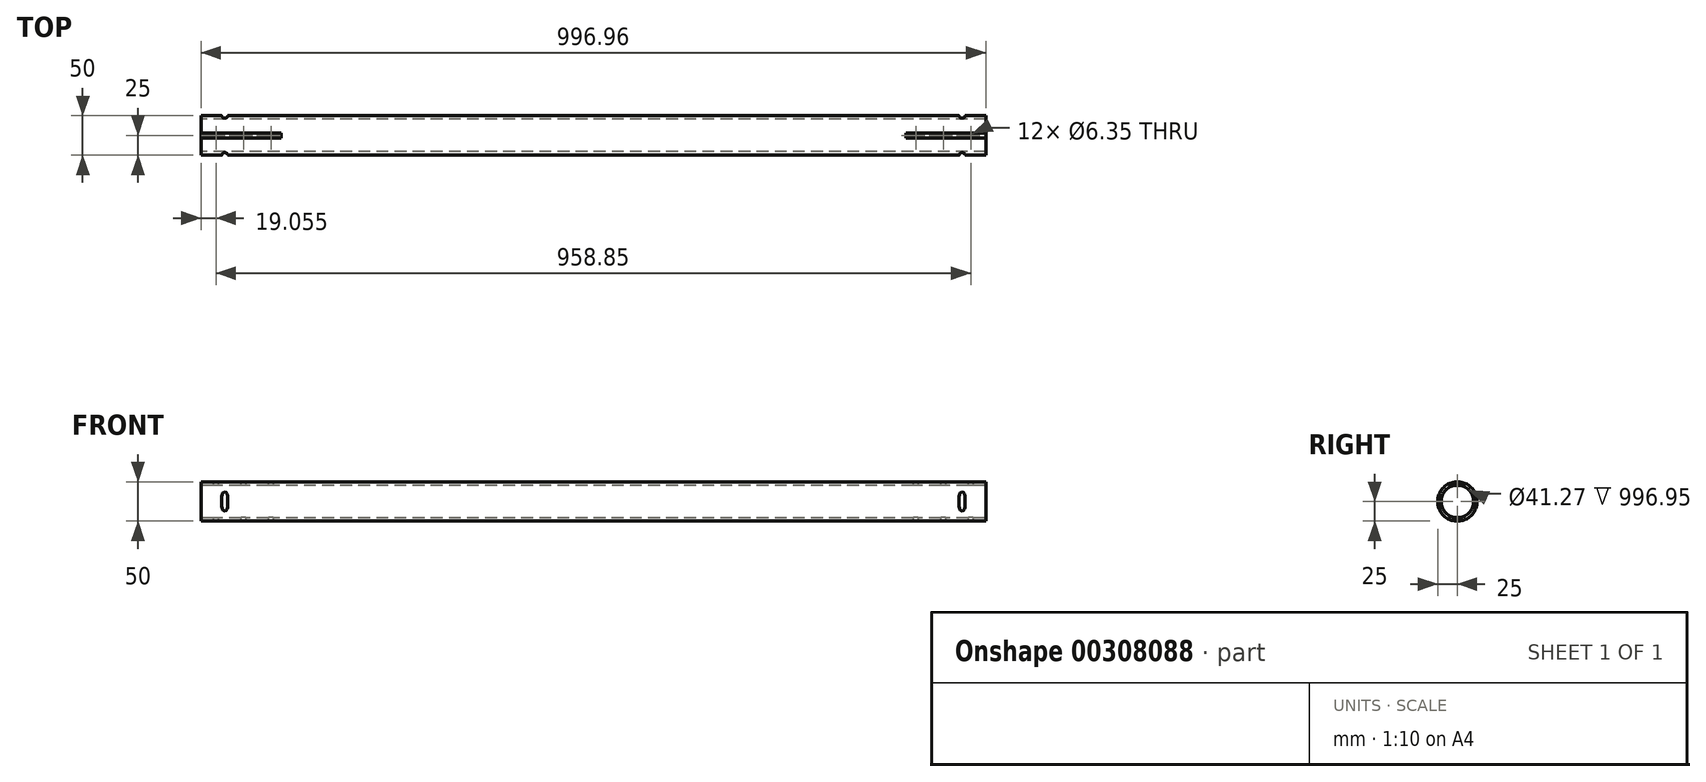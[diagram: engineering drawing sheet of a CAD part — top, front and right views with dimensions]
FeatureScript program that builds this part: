
annotation { "Feature Type Name" : "Feature", "Feature Type Description" : "" }
export const myFeature = defineFeature(function(context is Context, id is Id, definition is map)
    precondition{}
    {
        {
            var Q0;
            Q0=qCreatedBy(makeId("Right.planeOp"),FACE);
            var sketch = newSketch(context, id + "F0", { "sketchPlane" : qUnion([Q0])});
            skCircle(sketch, "E0", {"center": v(0, 0) * mm, "radius": 20.64 * mm});
            skCircle(sketch, "E1", {"center": v(0, 0) * mm, "radius": 25 * mm});
            skSolve(sketch);
        }
        {
            var Q0;
            Q0=qSketchRegion(id+"F0",true);
            extrude(context, id + "F1", {"entities" : qUnion([Q0]), "endBound" : BoundingType.SYMMETRIC, "depth" : 996.95 * mm, "offsetDistance" : 25.4 * mm});
        }
        {
            var Q0;
            Q0=makeQuery(id+"F1.opExtrude","CAP_FACE",FACE,{"disambiguationData":[OSD([sQuery(id+"F0.wireOp",EDGE,"E0"),sQuery(id+"F0.wireOp",EDGE,"E1")])],"isStart":false});
            var sketch = newSketch(context, id + "F2", { "sketchPlane" : qUnion([Q0])});
            skLineSegment(sketch, "E2", {"start": v(-25, 0) * mm, "end": v(25, 0) * mm, "construction": true});
            skLineSegment(sketch, "E3.bottom", {"start": v(-3.17, 26.39) * mm, "end": v(3.18, 26.39) * mm});
            skLineSegment(sketch, "E3.top", {"start": v(-3.17, 24.8) * mm, "end": v(3.18, 24.8) * mm});
            skLineSegment(sketch, "E3.left", {"start": v(-3.17, 26.39) * mm, "end": v(-3.17, 24.8) * mm});
            skLineSegment(sketch, "E3.right", {"start": v(3.18, 26.39) * mm, "end": v(3.18, 24.8) * mm});
            skLineSegment(sketch, "E4.MirrorCS", {"start": v(3.18, -26.39) * mm, "end": v(3.18, -24.8) * mm});
            skLineSegment(sketch, "E5.MirrorCS", {"start": v(-3.17, -26.39) * mm, "end": v(-3.17, -24.8) * mm});
            skLineSegment(sketch, "E6.MirrorCS", {"start": v(-3.17, -24.8) * mm, "end": v(3.18, -24.8) * mm});
            skLineSegment(sketch, "E7.MirrorCS", {"start": v(-3.17, -26.39) * mm, "end": v(3.18, -26.39) * mm});
            skSolve(sketch);
        }
        {
            var Q0;
            Q0=qSketchRegion(id+"F2",true);
            extrude(context, id + "F3", {"entities" : qUnion([Q0]), "operationType" : NewBodyOperationType.REMOVE, "oppositeDirection" : true, "depth" : 101.6 * mm, "offsetDistance" : 25.4 * mm});
        }
        {
            var Q0;
            Q0=makeQuery(id+"F1.opExtrude","CAP_FACE",FACE,{"disambiguationData":[OSD([sQuery(id+"F0.wireOp",EDGE,"E0"),sQuery(id+"F0.wireOp",EDGE,"E1")])],"isStart":true});
            var sketch = newSketch(context, id + "F4", { "sketchPlane" : qUnion([Q0])});
            skLineSegment(sketch, "E8.bottom", {"start": v(-3.17, 26.39) * mm, "end": v(3.18, 26.39) * mm});
            skLineSegment(sketch, "E8.top", {"start": v(-3.17, 24.8) * mm, "end": v(3.18, 24.8) * mm});
            skLineSegment(sketch, "E8.left", {"start": v(-3.17, 26.39) * mm, "end": v(-3.17, 24.8) * mm});
            skLineSegment(sketch, "E8.right", {"start": v(3.18, 26.39) * mm, "end": v(3.18, 24.8) * mm});
            skLineSegment(sketch, "E9", {"start": v(-25, 0) * mm, "end": v(25, 0) * mm, "construction": true});
            skLineSegment(sketch, "E10.MirrorCS", {"start": v(-3.17, -26.39) * mm, "end": v(-3.17, -24.8) * mm});
            skLineSegment(sketch, "E11.MirrorCS", {"start": v(3.18, -26.39) * mm, "end": v(3.18, -24.8) * mm});
            skLineSegment(sketch, "E12.MirrorCS", {"start": v(-3.17, -26.39) * mm, "end": v(3.18, -26.39) * mm});
            skLineSegment(sketch, "E13.MirrorCS", {"start": v(-3.17, -24.8) * mm, "end": v(3.18, -24.8) * mm});
            skSolve(sketch);
        }
        {
            var Q0;
            Q0=qSketchRegion(id+"F4",true);
            extrude(context, id + "F5", {"entities" : qUnion([Q0]), "operationType" : NewBodyOperationType.REMOVE, "oppositeDirection" : true, "depth" : 101.6 * mm, "offsetDistance" : 25.4 * mm});
        }
        {
            var Q0;
            Q0=makeQuery(id+"F5.boolean.opBoolean","COPY",FACE,{"derivedFrom":makeQuery(id+"F5.opExtrude","SWEPT_FACE",FACE,{"disambiguationData":[OSD([sQuery(id+"F4.wireOp",EDGE,"E8.top")])]})});
            var sketch = newSketch(context, id + "F6", { "sketchPlane" : qUnion([Q0])});
            skLineSegment(sketch, "E14", {"start": v(-498.48, 0) * mm, "end": v(-409.58, 0) * mm, "construction": true});
            skPoint(sketch, "E15", {"position": v(-479.43, 0) * mm});
            skPoint(sketch, "E16", {"position": v(-444.5, 0) * mm});
            skPoint(sketch, "E17", {"position": v(-409.58, 0) * mm});
            skLineSegment(sketch, "E18.MirrorCS", {"start": v(498.48, 0) * mm, "end": v(409.58, 0) * mm, "construction": true});
            skPoint(sketch, "E19.MirrorP", {"position": v(444.5, 0) * mm});
            skPoint(sketch, "E20.MirrorP", {"position": v(479.43, 0) * mm});
            skPoint(sketch, "E21.MirrorP", {"position": v(409.58, 0) * mm});
            skSolve(sketch);
        }
        {
            var Q0;
            Q0=sQuery(id+"F6.wireOp",VERTEX,"E15");
            var Q1;
            Q1=sQuery(id+"F6.wireOp",VERTEX,"E16");
            var Q2;
            Q2=sQuery(id+"F6.wireOp",VERTEX,"E17");
            var Q3;
            Q3=sQuery(id+"F6.wireOp",VERTEX,"E21.MirrorP");
            var Q4;
            Q4=sQuery(id+"F6.wireOp",VERTEX,"E19.MirrorP");
            var Q5;
            Q5=sQuery(id+"F6.wireOp",VERTEX,"E20.MirrorP");
            var Q6;
            Q6=makeQuery(id+"F1.opExtrude","SWEPT_BODY",BODY,{"disambiguationData":[OSD([sQuery(id+"F0.wireOp",EDGE,"E0"),sQuery(id+"F0.wireOp",EDGE,"E1")])]});
            hole(context, id + "F7", {"style" : HoleStyle.SIMPLE, "endStyle" : HoleEndStyle.THROUGH, "holeDiameter" : 6.35 * mm, "majorDiameter" : 6.35 * mm, "isTappedThrough" : true, "tappedDepth" : 12.7 * mm, "tapClearance" : 3, "locations" : qUnion([Q0, Q1, Q2, Q3, Q4, Q5]), "scope" : qUnion([Q6])});
        }
        {
            var Q0;
            {var subQ0=sQuery(id+"F0.wireOp",EDGE,"E1");var subQ1=makeQuery(id+"F5.boolean.opBoolean","COPY",FACE,{"derivedFrom":makeQuery(id+"F5.opExtrude","SWEPT_FACE",FACE,{"disambiguationData":[OSD([sQuery(id+"F4.wireOp",EDGE,"E8.top")])]})});Q0=makeQuery(id+"F7.hole-0.boolean.opBoolean","SPLIT",FACE,{"disambiguationData":[TD([makeQuery(id+"F1.opExtrude","CAP_FACE",FACE,{"disambiguationData":[OSD([sQuery(id+"F0.wireOp",EDGE,"E0"),subQ0])],"isStart":true})])],"derivedFrom":subQ1});}
            var sketch = newSketch(context, id + "F8", { "sketchPlane" : qUnion([Q0])});
            skCircle(sketch, "E22", {"center": v(-468.31, 25.8) * mm, "radius": 3.97 * mm});
            skCircle(sketch, "E23", {"center": v(-468.31, -25.8) * mm, "radius": 3.97 * mm});
            skCircle(sketch, "E24.MirrorC", {"center": v(468.31, 25.8) * mm, "radius": 3.97 * mm});
            skCircle(sketch, "E25.MirrorC", {"center": v(468.31, -25.8) * mm, "radius": 3.97 * mm});
            skSolve(sketch);
        }
        {
            var Q0;
            Q0=qSketchRegion(id+"F8",true);
            extrude(context, id + "F9", {"entities" : qUnion([Q0]), "operationType" : NewBodyOperationType.REMOVE, "endBound" : BoundingType.THROUGH_ALL, "oppositeDirection" : true, "depth" : 25.4 * mm, "offsetDistance" : 25.4 * mm});
        }
    });
